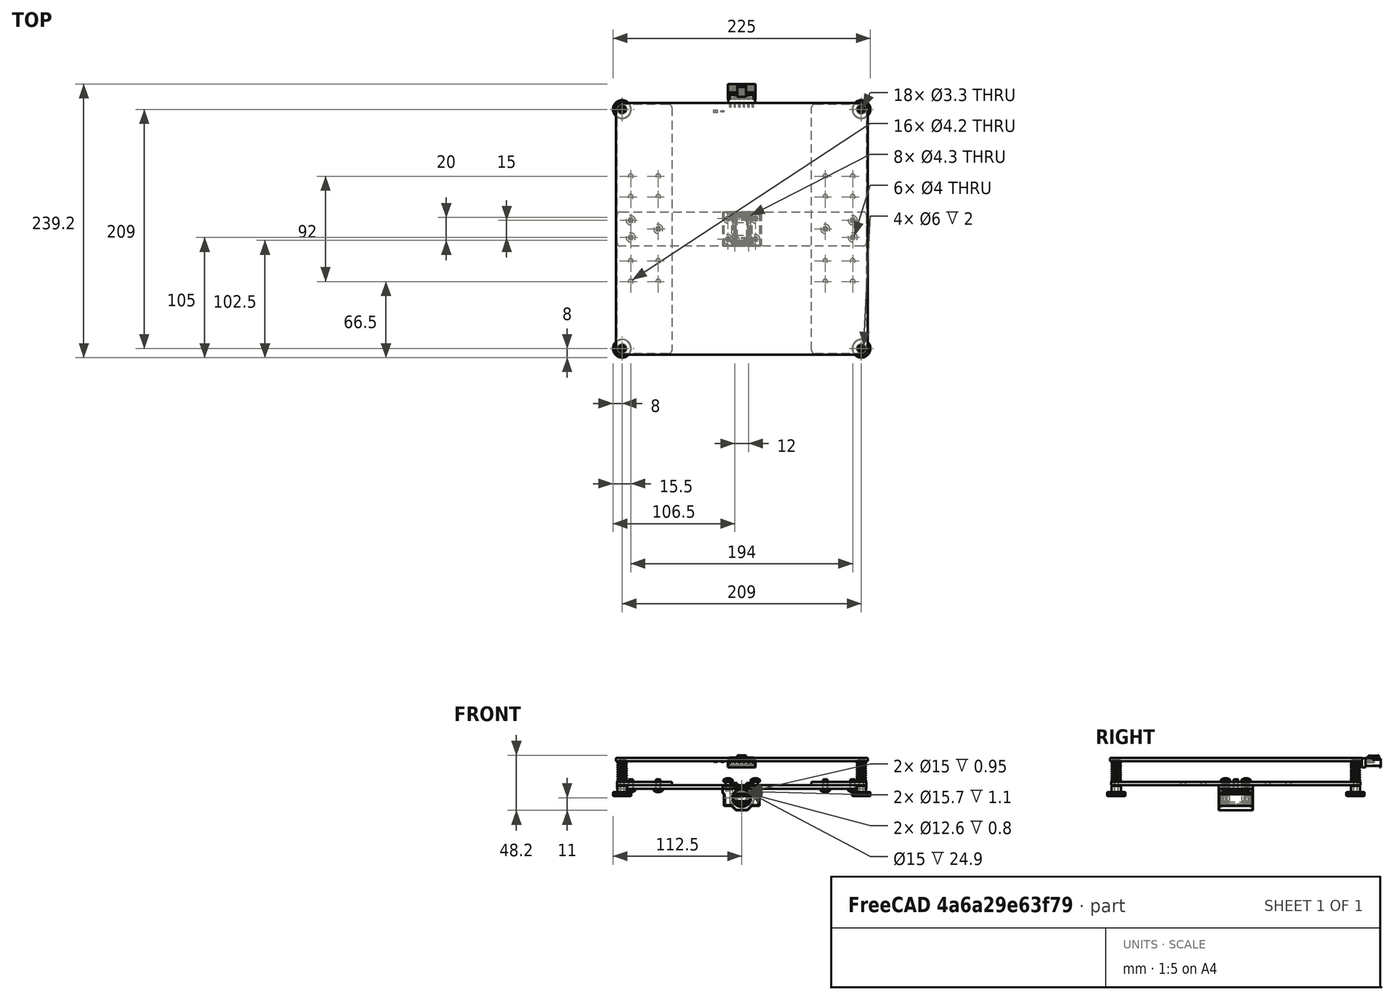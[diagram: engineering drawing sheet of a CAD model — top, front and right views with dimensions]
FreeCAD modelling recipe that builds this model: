
FCSTD DOCUMENT  (FreeCAD 0.18R16117 (Git))
Label: Y-Axis-Carrier
License: CreativeCommons Attribution-ShareAlike
LicenseURL: http://creativecommons.org/licenses/by-sa/4.0/
objects: Part::FeaturePython×34, Part::Feature×32, App::DocumentObjectGroup×5, App::Part×5
note: 66 computed .brp shape members not serialized (recipe doc carries the construction recipe); baked Part::Feature solids carry a one-line shape summary decoded from their .brp

FEATURE [Part::Feature] Body001002  label="Strut_vertical002"
  Placement = pos=(0,1.3e-14,11) rot=(0,0,1;3.14159rad)
  shape: bbox 48 x 218 x 3 mm, 23 faces (baked)
FEATURE [Part::Feature] Body001001  label="Strut_vertical001"
  Placement = pos=(0,0,11) rot=(0,0,1;0rad)
  shape: bbox 48 x 218 x 3 mm, 23 faces (baked)
FEATURE [Part::Feature] Body009  label="Strut_horizontal"
  Placement = pos=(0,0,8) rot=(0,0,1;0rad)
  shape: bbox 218 x 30 x 3 mm, 20 faces (baked)
FEATURE [Part::Feature] Body001031  label="Seeger-RingJ15_001"
  Placement = pos=(0,13,0) rot=(0,1,0;1.0472rad)
  shape: bbox 17.53 x 1 x 17.53 mm, 38 faces (baked)
FEATURE [Part::Feature] Body001032  label="Seeger-RingJ15_002"
  Placement = pos=(0,-13,0) rot=(0,0,1;0rad)
  shape: bbox 16.94 x 1 x 16.91 mm, 38 faces (baked)
FEATURE [Part::Feature] Body001030  label="SC8UU_001"
  shape: bbox 34 x 30 x 22 mm, 79 faces (baked)
FEATURE [Part::Feature] Body001033  label="SC8UU_002"
  shape: bbox 34 x 30 x 22 mm, 79 faces (baked)
FEATURE [Part::Feature] Body001036  label="Seeger-RingJ15_004"
  Placement = pos=(0,13,0) rot=(0,-1,0;1.8326rad)
  shape: bbox 17.24 x 1 x 16.94 mm, 38 faces (baked)
FEATURE [Part::Feature] Body001035  label="Seeger-RingJ15_003"
  Placement = pos=(0,-13,0) rot=(0,1,0;3.66519rad)
  shape: bbox 16.94 x 1 x 16.96 mm, 38 faces (baked)
FEATURE [Part::Feature] Body001037  label="Seeger-RingJ15_005"
  Placement = pos=(0,-13,0) rot=(0,-1,0;1.8326rad)
  shape: bbox 17.24 x 1 x 16.94 mm, 38 faces (baked)
FEATURE [Part::Feature] Body001038  label="Seeger-RingJ15_006"
  Placement = pos=(0,13,0) rot=(0,1,0;0.785398rad)
  shape: bbox 16.94 x 1 x 16.94 mm, 38 faces (baked)
FEATURE [Part::Feature] Body001043  label="Seeger-RingJ15_007"
  Placement = pos=(0,13,0) rot=(0,1,0;2.35619rad)
  shape: bbox 16.94 x 1 x 16.94 mm, 38 faces (baked)
FEATURE [Part::Feature] Body001040  label="SC8UU_003"
  shape: bbox 34 x 30 x 22 mm, 79 faces (baked)
FEATURE [Part::Feature] Body001044  label="Seeger-RingJ15_008"
  Placement = pos=(0,-13,0) rot=(0,1,0;1.5708rad)
  shape: bbox 16.91 x 1 x 16.94 mm, 38 faces (baked)
FEATURE [Part::Feature] Body001042  label="SC8UU_004"
  shape: bbox 34 x 30 x 22 mm, 79 faces (baked)
FEATURE [Part::Feature] Compound001  label="LM8UU_001"
  Placement = pos=(0,0,0) rot=(-1,0,0;1.5708rad)
  shape: bbox 15 x 24 x 15 mm, 36 faces, 2 solids (baked)
FEATURE [Part::Feature] Compound002  label="LM8UU_002"
  Placement = pos=(0,0,0) rot=(-1,0,0;1.5708rad)
  shape: bbox 15 x 24 x 15 mm, 36 faces, 2 solids (baked)
FEATURE [Part::Feature] Compound003  label="LM8UU_003"
  Placement = pos=(0,0,0) rot=(-1,0,0;1.5708rad)
  shape: bbox 15 x 24 x 15 mm, 36 faces, 2 solids (baked)
FEATURE [Part::Feature] Compound004  label="LM8UU_004"
  Placement = pos=(0,0,0) rot=(-1,0,0;1.5708rad)
  shape: bbox 15 x 24 x 15 mm, 36 faces, 2 solids (baked)
FEATURE [Part::Feature] Body001025  label="BeltClamp001"
  Placement = pos=(0,10,5.75) rot=(0,0,1;0rad)
  shape: bbox 21 x 9 x 4.5 mm, 8 faces (baked)
FEATURE [Part::Feature] Body001026  label="BeltClamp002"
  Placement = pos=(0,-10,5.75) rot=(0,0,1;0rad)
  shape: bbox 21 x 9 x 4.5 mm, 8 faces (baked)
FEATURE [Part::Feature] Body001027  label="BeltClamp003"
  Placement = pos=(0,10,-0.75) rot=(0,0,1;0rad)
  shape: bbox 21 x 9 x 4.5 mm, 8 faces (baked)
FEATURE [Part::Feature] Body001028  label="BeltClamp004"
  Placement = pos=(0,-10,-0.75) rot=(0,0,1;0rad)
  shape: bbox 21 x 9 x 4.5 mm, 8 faces (baked)
FEATURE [Part::FeaturePython] Screw  label="M4x16-Screw_001"  # Fasteners workbench fastener (typed FeaturePython)
  Placement = pos=(6,-10,-3) rot=(1,0,0;3.14159rad)
  diameter = 6
  invert = false
  length = 6
  matchOuter = false
  offset = 0
  thread = false
  type = 16
FEATURE [Part::FeaturePython] Screw001  label="M4x16-Screw_002"  # Fasteners workbench fastener (typed FeaturePython)
  Placement = pos=(-6,-10,-3) rot=(1,0,0;3.14159rad)
  diameter = 6
  invert = false
  length = 6
  matchOuter = false
  offset = 0
  thread = false
  type = 16
FEATURE [Part::FeaturePython] Screw002  label="M4x16-Screw_003"  # Fasteners workbench fastener (typed FeaturePython)
  Placement = pos=(6,10,-3) rot=(1,0,0;3.14159rad)
  diameter = 6
  invert = false
  length = 6
  matchOuter = false
  offset = 0
  thread = false
  type = 16
FEATURE [Part::FeaturePython] Screw003  label="M4x16-Screw_004"  # Fasteners workbench fastener (typed FeaturePython)
  Placement = pos=(-6,10,-3) rot=(1,0,0;3.14159rad)
  diameter = 6
  invert = false
  length = 6
  matchOuter = false
  offset = 0
  thread = false
  type = 16
FEATURE [App::DocumentObjectGroup] Group003  label="BeltClamps"
  Group = -> [Body001025,Body001026,Body001027,Body001028,Screw,Screw001,Screw002,Screw003]
FEATURE [Part::FeaturePython] Screw004  label="M4x8-Screw_001"  # Fasteners workbench fastener (typed FeaturePython)
  Placement = pos=(97,7.5,8) rot=(1,0,0;3.14159rad)
  diameter = 6
  invert = false
  length = 2
  matchOuter = false
  offset = 0
  thread = false
  type = 16
FEATURE [Part::FeaturePython] Screw005  label="M4x8-Screw_002"  # Fasteners workbench fastener (typed FeaturePython)
  Placement = pos=(97,-7.5,8) rot=(1,0,0;3.14159rad)
  diameter = 6
  invert = false
  length = 2
  matchOuter = false
  offset = 0
  thread = false
  type = 16
FEATURE [Part::FeaturePython] Screw006  label="M4x8-Screw_003"  # Fasteners workbench fastener (typed FeaturePython)
  Placement = pos=(73,2e-15,8) rot=(1,0,0;3.14159rad)
  diameter = 6
  invert = false
  length = 2
  matchOuter = false
  offset = 0
  thread = false
  type = 16
FEATURE [Part::FeaturePython] Screw007  label="M4x8-Screw_004"  # Fasteners workbench fastener (typed FeaturePython)
  Placement = pos=(-73,2e-15,8) rot=(1,0,0;3.14159rad)
  diameter = 6
  invert = false
  length = 2
  matchOuter = false
  offset = 0
  thread = false
  type = 16
FEATURE [Part::FeaturePython] Screw008  label="M4x8-Screw_005"  # Fasteners workbench fastener (typed FeaturePython)
  Placement = pos=(-97,7.5,8) rot=(1,0,0;3.14159rad)
  diameter = 6
  invert = false
  length = 2
  matchOuter = false
  offset = 0
  thread = false
  type = 16
FEATURE [Part::FeaturePython] Screw009  label="M4x8-Screw_006"  # Fasteners workbench fastener (typed FeaturePython)
  Placement = pos=(-97,-7.5,8) rot=(1,0,0;3.14159rad)
  diameter = 6
  invert = false
  length = 2
  matchOuter = false
  offset = 0
  thread = false
  type = 16
FEATURE [App::DocumentObjectGroup] Group001  label="H-Holder"
  Group = -> [Body009,Body001001,Body001002,Screw004,Screw005,Screw006,Screw007,Screw008,Screw009,Group003]
FEATURE [Part::FeaturePython] Screw010  label="M4x8-Screw"  # Fasteners workbench fastener (typed FeaturePython)
  Placement = pos=(-12,9,14) rot=(0,0,1;0rad)
  diameter = 6
  invert = false
  length = 2
  matchOuter = false
  offset = 0
  thread = false
  type = 16
FEATURE [Part::FeaturePython] Screw011  label="M4x8-Screw031"  # Fasteners workbench fastener (typed FeaturePython)
  Placement = pos=(-12,-9,14) rot=(1,0,0;0rad)
  diameter = 6
  invert = false
  length = 2
  matchOuter = false
  offset = 0
  thread = false
  type = 16
FEATURE [Part::FeaturePython] Screw012  label="M4x8-Screw033"  # Fasteners workbench fastener (typed FeaturePython)
  Placement = pos=(12,9,14) rot=(1,0,0;0rad)
  diameter = 6
  invert = false
  length = 2
  matchOuter = false
  offset = 0
  thread = false
  type = 16
FEATURE [Part::FeaturePython] Screw013  label="M4x8-Screw032"  # Fasteners workbench fastener (typed FeaturePython)
  Placement = pos=(12,-9,14) rot=(1,0,0;0rad)
  diameter = 6
  invert = false
  length = 2
  matchOuter = false
  offset = 0
  thread = false
  type = 16
FEATURE [App::Part] Part009  label="SCS8UU_001"
  Group = -> [Body001030,Compound001,Body001031,Body001032,Screw010,Screw011,Screw012,Screw013]
  Origin = -> Origin009
  Placement = pos=(-85,-37,0) rot=(0,0,1;0rad)
FEATURE [Part::FeaturePython] Screw014  label="M4x8-Screw034"  # Fasteners workbench fastener (typed FeaturePython)
  Placement = pos=(-12,9,14) rot=(1,0,0;0rad)
  diameter = 6
  invert = false
  length = 2
  matchOuter = false
  offset = 0
  thread = false
  type = 16
FEATURE [Part::FeaturePython] Screw015  label="M4x8-Screw037"  # Fasteners workbench fastener (typed FeaturePython)
  Placement = pos=(-12,-9,14) rot=(1,0,0;0rad)
  diameter = 6
  invert = false
  length = 2
  matchOuter = false
  offset = 0
  thread = false
  type = 16
FEATURE [Part::FeaturePython] Screw016  label="M4x8-Screw036"  # Fasteners workbench fastener (typed FeaturePython)
  Placement = pos=(12,9,14) rot=(1,0,0;0rad)
  diameter = 6
  invert = false
  length = 2
  matchOuter = false
  offset = 0
  thread = false
  type = 16
FEATURE [Part::FeaturePython] Screw017  label="M4x8-Screw035"  # Fasteners workbench fastener (typed FeaturePython)
  Placement = pos=(12,-9,14) rot=(1,0,0;0rad)
  diameter = 6
  invert = false
  length = 2
  matchOuter = false
  offset = 0
  thread = false
  type = 16
FEATURE [App::Part] Part010  label="SCS8UU_002"
  Group = -> [Body001033,Compound002,Body001035,Body001036,Screw014,Screw015,Screw016,Screw017]
  Origin = -> Origin010
  Placement = pos=(-85,37,0) rot=(0,0,1;0rad)
FEATURE [Part::FeaturePython] Screw018  label="M4x8-Screw039"  # Fasteners workbench fastener (typed FeaturePython)
  Placement = pos=(-12,9,14) rot=(1,0,0;0rad)
  diameter = 6
  invert = false
  length = 2
  matchOuter = false
  offset = 0
  thread = false
  type = 16
FEATURE [Part::FeaturePython] Screw019  label="M4x8-Screw038"  # Fasteners workbench fastener (typed FeaturePython)
  Placement = pos=(-12,-9,14) rot=(1,0,0;0rad)
  diameter = 6
  invert = false
  length = 2
  matchOuter = false
  offset = 0
  thread = false
  type = 16
FEATURE [Part::FeaturePython] Screw020  label="M4x8-Screw041"  # Fasteners workbench fastener (typed FeaturePython)
  Placement = pos=(12,9,14) rot=(1,0,0;0rad)
  diameter = 6
  invert = false
  length = 2
  matchOuter = false
  offset = 0
  thread = false
  type = 16
FEATURE [Part::FeaturePython] Screw021  label="M4x8-Screw040"  # Fasteners workbench fastener (typed FeaturePython)
  Placement = pos=(12,-9,14) rot=(1,0,0;0rad)
  diameter = 6
  invert = false
  length = 2
  matchOuter = false
  offset = 0
  thread = false
  type = 16
FEATURE [App::Part] Part011  label="SCS8UU_003"
  Group = -> [Body001040,Compound003,Body001037,Body001038,Screw018,Screw019,Screw020,Screw021]
  Origin = -> Origin011
  Placement = pos=(85,37,0) rot=(0,0,1;0rad)
FEATURE [Part::FeaturePython] Screw022  label="M4x8-Screw042"  # Fasteners workbench fastener (typed FeaturePython)
  Placement = pos=(-12,9,14) rot=(1,0,0;0rad)
  diameter = 6
  invert = false
  length = 2
  matchOuter = false
  offset = 0
  thread = false
  type = 16
FEATURE [Part::FeaturePython] Screw023  label="M4x8-Screw045"  # Fasteners workbench fastener (typed FeaturePython)
  Placement = pos=(-12,-9,14) rot=(1,0,0;0rad)
  diameter = 6
  invert = false
  length = 2
  matchOuter = false
  offset = 0
  thread = false
  type = 16
FEATURE [Part::FeaturePython] Screw024  label="M4x8-Screw044"  # Fasteners workbench fastener (typed FeaturePython)
  Placement = pos=(12,9,14) rot=(1,0,0;0rad)
  diameter = 6
  invert = false
  length = 2
  matchOuter = false
  offset = 0
  thread = false
  type = 16
FEATURE [Part::FeaturePython] Screw025  label="M4x8-Screw043"  # Fasteners workbench fastener (typed FeaturePython)
  Placement = pos=(12,-9,14) rot=(1,0,0;0rad)
  diameter = 6
  invert = false
  length = 2
  matchOuter = false
  offset = 0
  thread = false
  type = 16
FEATURE [App::Part] Part012  label="SCS8UU_004"
  Group = -> [Body001042,Compound004,Body001043,Body001044,Screw022,Screw023,Screw024,Screw025]
  Origin = -> Origin012
  Placement = pos=(85,-37,0) rot=(0,0,1;0rad)
FEATURE [App::DocumentObjectGroup] Group002  label="Linear-Bearings"
  Group = -> [Part009,Part010,Part011,Part012]
FEATURE [App::DocumentObjectGroup] Group  label="carrying_frame"
  Group = -> [Group001,Group002]
FEATURE [Part::Feature] Fusion002  label="heat-plate_220x220"
  Placement = pos=(0,0,32) rot=(0,0,1;0rad)
  shape: bbox 220 x 236.7 x 10.5 mm, 302 faces (baked)
FEATURE [Part::Feature] Body001045  label="Spring_8x1x24/18_001"
  Placement = pos=(104.5,104.5,14) rot=(0,0,1;0rad)
  shape: bbox 8.219 x 8.219 x 18.9 mm, 12 faces (baked)
FEATURE [Part::Feature] Body001046  label="Spring_8x1x24/18_002"
  Placement = pos=(-104.5,104.5,14) rot=(0,0,1;0rad)
  shape: bbox 8.219 x 8.219 x 18.9 mm, 12 faces (baked)
FEATURE [Part::Feature] Body001047  label="Spring_8x1x24/18_003"
  Placement = pos=(104.5,-104.5,14) rot=(0,0,1;0rad)
  shape: bbox 8.219 x 8.219 x 18.9 mm, 12 faces (baked)
FEATURE [Part::Feature] Body001048  label="Spring_8x1x24/18_004"
  Placement = pos=(-104.5,-104.5,14) rot=(0,0,1;0rad)
  shape: bbox 8.219 x 8.219 x 18.9 mm, 12 faces (baked)
FEATURE [Part::FeaturePython] Nut  label="M3-Nut"  # Fasteners workbench fastener (typed FeaturePython)
  Placement = pos=(-104.5,104.5,29.6) rot=(0,0,1;0rad)
  diameter = 4
  invert = false
  matchOuter = false
  offset = 0
  thread = false
  type = 4
FEATURE [Part::FeaturePython] Nut001  label="M3-Nut005"  # Fasteners workbench fastener (typed FeaturePython)
  Placement = pos=(104.5,104.5,29.6) rot=(0,0,1;0rad)
  diameter = 4
  invert = false
  matchOuter = false
  offset = 0
  thread = false
  type = 4
FEATURE [Part::FeaturePython] Nut002  label="M3-Nut004"  # Fasteners workbench fastener (typed FeaturePython)
  Placement = pos=(-104.5,-104.5,29.6) rot=(0,0,1;0rad)
  diameter = 4
  invert = false
  matchOuter = false
  offset = 0
  thread = false
  type = 4
FEATURE [Part::FeaturePython] Nut003  label="M3-Nut003"  # Fasteners workbench fastener (typed FeaturePython)
  Placement = pos=(104.5,-104.5,29.6) rot=(0,0,1;0rad)
  diameter = 4
  invert = false
  matchOuter = false
  offset = 0
  thread = false
  type = 4
FEATURE [Part::FeaturePython] Screw026  label="M3x30-Screw"  # Fasteners workbench fastener (typed FeaturePython)
  Placement = pos=(-104.5,104.5,34.5) rot=(0,0,1;0rad)
  diameter = 4
  invert = false
  length = 10
  matchOuter = false
  offset = 0
  thread = false
  type = 17
FEATURE [Part::FeaturePython] Screw027  label="M3x30-Screw005"  # Fasteners workbench fastener (typed FeaturePython)
  Placement = pos=(104.5,104.5,34.5) rot=(0,0,1;0rad)
  diameter = 4
  invert = false
  length = 10
  matchOuter = false
  offset = 0
  thread = false
  type = 17
FEATURE [Part::FeaturePython] Screw028  label="M3x30-Screw004"  # Fasteners workbench fastener (typed FeaturePython)
  Placement = pos=(-104.5,-104.5,34.5) rot=(0,0,1;0rad)
  diameter = 4
  invert = false
  length = 10
  matchOuter = false
  offset = 0
  thread = false
  type = 17
FEATURE [Part::FeaturePython] Screw029  label="M3x30-Screw003"  # Fasteners workbench fastener (typed FeaturePython)
  Placement = pos=(104.5,-104.5,34.5) rot=(0,0,1;0rad)
  diameter = 4
  invert = false
  length = 10
  matchOuter = false
  offset = 0
  thread = false
  type = 17
FEATURE [Part::Feature] Body001049  label="Thumb-Wheel_M4_001"
  Placement = pos=(-104.5,-104.5,1.5) rot=(0,0,1;0rad)
  shape: bbox 16 x 16 x 9.5 mm, 281 faces (baked)
FEATURE [Part::Feature] Body001051  label="Thumb-Wheel_M4_003"
  Placement = pos=(-104.5,104.5,1.5) rot=(0,0,1;0rad)
  shape: bbox 16 x 16 x 9.5 mm, 281 faces (baked)
FEATURE [Part::Feature] Body001052  label="Thumb-Wheel_M4_004"
  Placement = pos=(104.5,104.5,1.5) rot=(0,0,1;0rad)
  shape: bbox 16 x 16 x 9.5 mm, 281 faces (baked)
FEATURE [Part::Feature] Body001050  label="Thumb-Wheel_M4_002"
  Placement = pos=(104.5,-104.5,1.5) rot=(0,0,1;0rad)
  shape: bbox 16 x 16 x 9.5 mm, 281 faces (baked)
FEATURE [App::DocumentObjectGroup] Group004  label="heated_bed"
  Group = -> [Fusion002,Screw026,Screw027,Screw028,Screw029,Nut,Nut001,Nut002,Nut003,Body001045,Body001046,Body001047,Body001048,Body001049,Body001051,Body001052,Body001050]
FEATURE [App::Part] Part  label="Y-Axis-Carrier_Assembly"
  Group = -> [Group,Body009,Body001001,Body001002,Group001,Group002,Part009,Part010,Part011,Part012,Body001026,Body001027,Body001025,Body001028,Group003,Screw,Screw001,Screw002,Screw003,Screw004,Screw005,Screw006,Screw007,Screw008,Screw009,Group004,Fusion002,Screw026,Screw027,Screw028,Screw029,Nut,Nut001,Nut002,Nut003,Body001045,Body001046,Body001047,Body001048,Body001049,Body001051,Body001052,Body001050]
  Origin = -> Origin
